# Revit family: Bisley_Caddy
name_source: partatom
category: Furniture
revit_build: Autodesk Revit 2018 (Build: 20170223_1515(x64)
units: mm (PartAtom-declared; Revit-internal decimal feet)

## family parameters
Always vertical = No
Cut with Voids When Loaded = No
OmniClass Number = 23.40.20.00
OmniClass Title = General Furniture and Specialties
Room Calculation Point = No
Shared = No
Work Plane-Based = No

## types (6) — shared parameters
Bisley_Depth = 491 mm  [stored 1.61089 ft]
Bisley_Height = 563 mm
Category = Furniture
Description = -
Manufacturer = Bisley
ManufacturerName = Bisley
Model = -
Type Comments = -
URL = www.bisley.com
Uniclass2015Code = Pr_40_30_78
Uniclass2015Title = Shelves and storage units
Uniclass2015Version = v1.5
WarrantyDurationUnit = 5 Years

## per-type parameters (varying)
| type | Bisley_Width | LH | RH |
| CADM08LH v2 | 800 mm  [stored 2.62467 ft] | Yes | No |
| CADM09LH v2 | 900 mm | Yes | No |
| CADM10LH v2 | 1000 mm  [stored 3.28084 ft] | Yes | No |
| CADM08RH v2 | 800 mm  [stored 2.62467 ft] | No | Yes |
| CADM09RH v2 | 900 mm | No | Yes |
| CADM10RH v2 | 1000 mm  [stored 3.28084 ft] | No | Yes |

note: [stored X ft] marks values corroborated as IEEE doubles in the binary element streams (Revit-internal decimal feet)

## geometry (parser evidence)
native form markers: Sweep x8
no freeform markers — native parametric forms only
